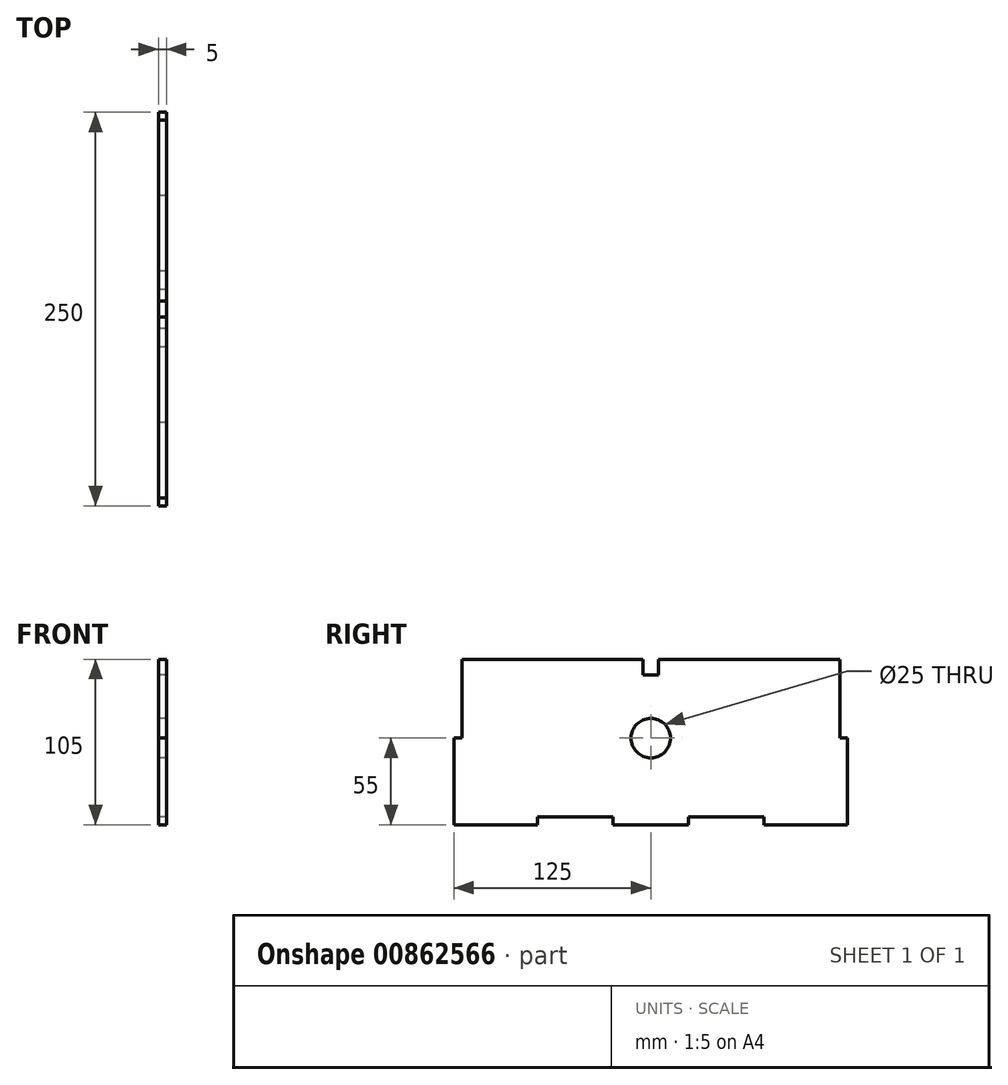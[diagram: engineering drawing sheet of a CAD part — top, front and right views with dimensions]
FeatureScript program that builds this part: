
annotation { "Feature Type Name" : "Feature", "Feature Type Description" : "" }
export const myFeature = defineFeature(function(context is Context, id is Id, definition is map)
    precondition{}
    {
        {
            var Q0;
            Q0=qCreatedBy(makeId("Right.planeOp"),FACE);
            var sketch = newSketch(context, id + "F0", { "sketchPlane" : qUnion([Q0])});
            skLineSegment(sketch, "E0.bottom", {"start": v(125, -50) * mm, "end": v(-125, -50) * mm});
            skLineSegment(sketch, "E0.top", {"start": v(125, 50) * mm, "end": v(5, 50) * mm});
            skLineSegment(sketch, "E0.left", {"start": v(125, -50) * mm, "end": v(125, 0) * mm});
            skLineSegment(sketch, "E0.right", {"start": v(-125, -50) * mm, "end": v(-125, 0) * mm});
            skPoint(sketch, "E0.middle", {"position": v(0, 0) * mm});
            skLineSegment(sketch, "E1", {"start": v(-125, -50) * mm, "end": v(-125, -55) * mm});
            skLineSegment(sketch, "E2", {"start": v(-125, -55) * mm, "end": v(-72, -55) * mm});
            skLineSegment(sketch, "E3", {"start": v(-72, -55) * mm, "end": v(-72, -50) * mm});
            skLineSegment(sketch, "E4", {"start": v(-72, -55) * mm, "end": v(-24, -55) * mm, "construction": true});
            skLineSegment(sketch, "E5", {"start": v(-24, -55) * mm, "end": v(-24, -50) * mm});
            skLineSegment(sketch, "E6", {"start": v(-24, -55) * mm, "end": v(24, -55) * mm});
            skLineSegment(sketch, "E7", {"start": v(24, -55) * mm, "end": v(24, -50) * mm});
            skLineSegment(sketch, "E8.MirrorCS", {"start": v(125, -55) * mm, "end": v(72, -55) * mm});
            skLineSegment(sketch, "E9.MirrorCS", {"start": v(72, -55) * mm, "end": v(72, -50) * mm});
            skLineSegment(sketch, "E10.MirrorCS", {"start": v(125, -50) * mm, "end": v(125, -55) * mm});
            skCircle(sketch, "E11", {"center": v(0, 0) * mm, "radius": 12.5 * mm});
            skLineSegment(sketch, "E12", {"start": v(120, 50) * mm, "end": v(120, 0) * mm});
            skLineSegment(sketch, "E13", {"start": v(120, 0) * mm, "end": v(125, 0) * mm});
            skLineSegment(sketch, "E14.MirrorCS", {"start": v(-120, 50) * mm, "end": v(-120, 0) * mm});
            skLineSegment(sketch, "E15.MirrorCS", {"start": v(-120, 0) * mm, "end": v(-125, 0) * mm});
            skLineSegment(sketch, "E16", {"start": v(-5, 50) * mm, "end": v(-5, 40) * mm});
            skLineSegment(sketch, "E17", {"start": v(-5, 40) * mm, "end": v(0, 40) * mm});
            skLineSegment(sketch, "E18.MirrorCS", {"start": v(5, 40) * mm, "end": v(0, 40) * mm});
            skLineSegment(sketch, "E19.MirrorCS", {"start": v(5, 50) * mm, "end": v(5, 40) * mm});
            skLineSegment(sketch, "E20.trimOffspring", {"start": v(-5, 50) * mm, "end": v(-125, 50) * mm});
            skSolve(sketch);
        }
        {
            var Q0;
            Q0 = qSketchRegion(id + "F0", true);
            extrude(context, id + "F1", {"entities" : qUnion([Q0]), "depth" : 5 * mm, "offsetDistance" : 25 * mm});
        }
    });
